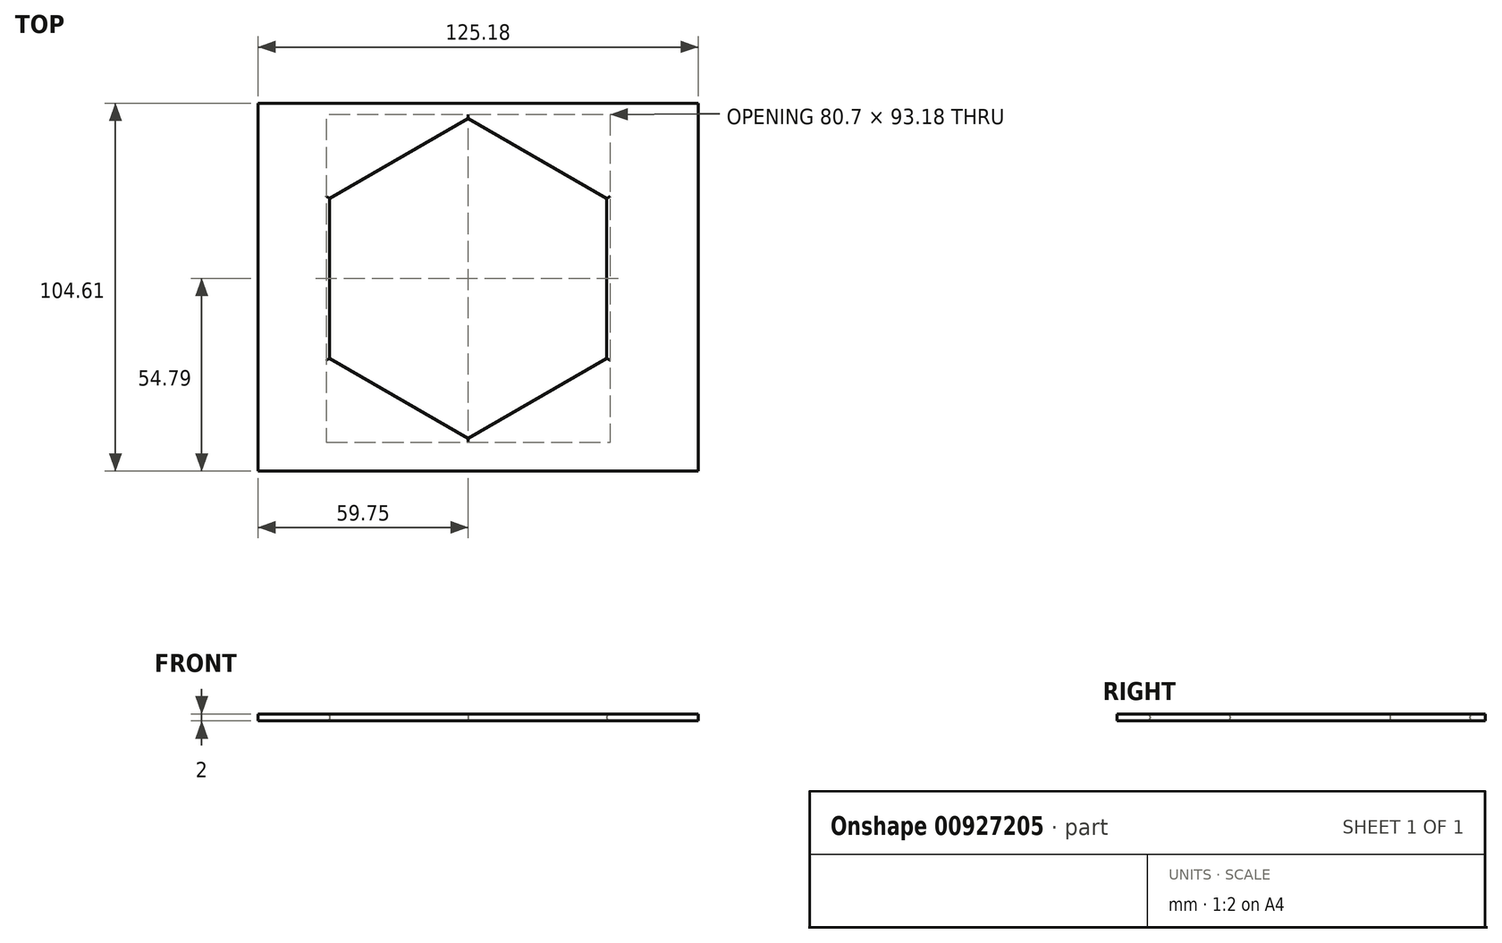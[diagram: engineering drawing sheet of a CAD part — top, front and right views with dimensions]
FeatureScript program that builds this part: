
annotation { "Feature Type Name" : "Feature", "Feature Type Description" : "" }
export const myFeature = defineFeature(function(context is Context, id is Id, definition is map)
    precondition{}
    {
        {
            var Q0;
            Q0=qCreatedBy(makeId("Top.planeOp"),FACE);
            var sketch = newSketch(context, id + "F0", { "sketchPlane" : qUnion([Q0])});
            skLineSegment(sketch, "E0.bottom", {"start": v(-59.75, 49.82) * mm, "end": v(65.43, 49.82) * mm});
            skLineSegment(sketch, "E0.top", {"start": v(-59.75, -54.79) * mm, "end": v(65.43, -54.79) * mm});
            skLineSegment(sketch, "E0.left", {"start": v(-59.75, 49.82) * mm, "end": v(-59.75, -54.79) * mm});
            skLineSegment(sketch, "E0.right", {"start": v(65.43, 49.82) * mm, "end": v(65.43, -54.79) * mm});
            skCircle(sketch, "E1.cCircle", {"center": v(0, 0) * mm, "radius": 39.35 * mm, "construction": true});
            skLineSegment(sketch, "E1.0", {"start": v(39.35, -22.72) * mm, "end": v(0, -45.44) * mm});
            skLineSegment(sketch, "E1.1", {"start": v(0, -45.44) * mm, "end": v(-39.35, -22.72) * mm});
            skLineSegment(sketch, "E1.2", {"start": v(-39.35, -22.72) * mm, "end": v(-39.35, 22.72) * mm});
            skLineSegment(sketch, "E1.3", {"start": v(-39.35, 22.72) * mm, "end": v(0, 45.44) * mm});
            skLineSegment(sketch, "E1.4", {"start": v(0, 45.44) * mm, "end": v(39.35, 22.72) * mm});
            skLineSegment(sketch, "E1.5", {"start": v(39.35, 22.72) * mm, "end": v(39.35, -22.72) * mm});
            skPoint(sketch, "E1.0.midPoint", {"position": v(19.67, -34.08) * mm});
            skSolve(sketch);
        }
        {
            var Q0;
            Q0=makeQuery(id+"F0.imprint","IMPRINT",FACE,{"disambiguationData":[TD([[makeQuery(id+"F0.imprint","IMPRINT",EDGE,{"derivedFrom":sQuery(id+"F0.wireOp",EDGE,"E0.bottom")}),-1.0]])]});
            extrude(context, id + "F1", {"entities" : qUnion([Q0]), "depth" : 2 * mm, "offsetDistance" : 25 * mm});
        }
        {
            var Q0;
            Q0=makeQuery(id+"F1.opExtrude","CAP_EDGE",EDGE,{"disambiguationData":[OSD([sQuery(id+"F0.wireOp",EDGE,"E1.1")])],"isStart":false});
            var Q1;
            Q1=makeQuery(id+"F1.opExtrude","CAP_EDGE",EDGE,{"disambiguationData":[OSD([sQuery(id+"F0.wireOp",EDGE,"E1.1")])],"isStart":true});
            fillet(context, id + "F2", {"entities" : qUnion([Q0, Q1]), "radius" : 1 * mm, "tangentPropagation" : true, "allowEdgeOverflow" : false});
        }
        {
            var Q0;
            Q0=makeQuery(id+"F1.opExtrude","CAP_EDGE",EDGE,{"disambiguationData":[OSD([sQuery(id+"F0.wireOp",EDGE,"E1.2")])],"isStart":false});
            var Q1;
            Q1=makeQuery(id+"F1.opExtrude","CAP_EDGE",EDGE,{"disambiguationData":[OSD([sQuery(id+"F0.wireOp",EDGE,"E1.2")])],"isStart":true});
            fillet(context, id + "F3", {"entities" : qUnion([Q0, Q1]), "radius" : 1 * mm, "tangentPropagation" : true, "allowEdgeOverflow" : false});
        }
        {
            var Q0;
            Q0=makeQuery(id+"F1.opExtrude","CAP_EDGE",EDGE,{"disambiguationData":[OSD([sQuery(id+"F0.wireOp",EDGE,"E1.0")])],"isStart":false});
            var Q1;
            Q1=makeQuery(id+"F1.opExtrude","CAP_EDGE",EDGE,{"disambiguationData":[OSD([sQuery(id+"F0.wireOp",EDGE,"E1.0")])],"isStart":true});
            fillet(context, id + "F4", {"entities" : qUnion([Q0, Q1]), "radius" : 1 * mm, "allowEdgeOverflow" : false});
        }
        {
            var Q0;
            Q0=makeQuery(id+"F1.opExtrude","CAP_EDGE",EDGE,{"disambiguationData":[OSD([sQuery(id+"F0.wireOp",EDGE,"E1.5")])],"isStart":false});
            var Q1;
            Q1=makeQuery(id+"F1.opExtrude","CAP_EDGE",EDGE,{"disambiguationData":[OSD([sQuery(id+"F0.wireOp",EDGE,"E1.5")])],"isStart":true});
            fillet(context, id + "F5", {"entities" : qUnion([Q0, Q1]), "radius" : 1 * mm, "allowEdgeOverflow" : false});
        }
        {
            var Q0;
            Q0=makeQuery(id+"F1.opExtrude","CAP_EDGE",EDGE,{"disambiguationData":[OSD([sQuery(id+"F0.wireOp",EDGE,"E1.3")])],"isStart":false});
            var Q1;
            Q1=makeQuery(id+"F1.opExtrude","CAP_EDGE",EDGE,{"disambiguationData":[OSD([sQuery(id+"F0.wireOp",EDGE,"E1.3")])],"isStart":true});
            fillet(context, id + "F6", {"entities" : qUnion([Q0, Q1]), "radius" : 1 * mm, "allowEdgeOverflow" : false});
        }
        {
            var Q0;
            Q0=makeQuery(id+"F1.opExtrude","CAP_EDGE",EDGE,{"disambiguationData":[OSD([sQuery(id+"F0.wireOp",EDGE,"E1.4")])],"isStart":false});
            var Q1;
            Q1=makeQuery(id+"F1.opExtrude","CAP_EDGE",EDGE,{"disambiguationData":[OSD([sQuery(id+"F0.wireOp",EDGE,"E1.4")])],"isStart":true});
            fillet(context, id + "F7", {"entities" : qUnion([Q0, Q1]), "radius" : 1 * mm, "tangentPropagation" : true, "allowEdgeOverflow" : false});
        }
    });
